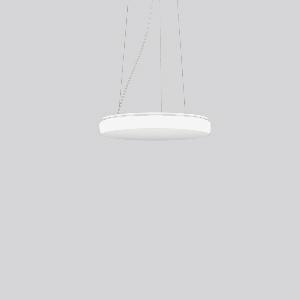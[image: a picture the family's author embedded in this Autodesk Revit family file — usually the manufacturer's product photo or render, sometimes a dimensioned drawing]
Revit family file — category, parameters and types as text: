
# Revit family: flat_polymero_kreis_slim_312090_002_2_f830
name_source: partatom
category: Lighting Fixtures
units: mm (PartAtom-declared; Revit-internal decimal feet)

## family parameters
Cut with Voids When Loaded = No
Host = Face
Light Source = No
Part Type = Normal
Room Calculation Point = No
Round Connector Dimension = Use Diameter
Shared = No

## types (1)
- FLAT POLYMERO KREIS SLIM (1 x LED Modul 830, 2000 lm, 3000)
    Apparent Load = 19 VA
    CIE Flux Codes = 44 76 94 92 100
    Color Rendering = 80
    Color Temperature = 3000
    Default Elevation = 1800 mm
    Description = Series: FLAT POLYMERO KREIS SLIM
Decorative round LED pendant luminaire. Base and canopy: metal, powder-coated, white. Canopy Ø 205 mm, h 35 mm. Diffuser made of plastic (polycarbonate), opal, shockproof. Diffuser fastening: patented push system. Homogeneous and smooth light distribution. Suitable for pendant. 3-point steel cable suspension, steplessly adjustable. Special lengths available on request. 
Colour: white
Diameter: 460 mm
Height: 68 mm
Suspension length: 200-1300 mm
Lamp: LED
Socket: without socket
Colour temperature: 3000K
Colour rendering index (CRI): 80
System power: 19 W
Rated luminous flux: 2000 lm
Luminous efficiency: 105 lm/W
Control gear: AC Strom, dim.Ph.an-/abschnitt
Protection class: I
Type of protection: IP 40
    Height = 68 mm
    Lamp = 1 x LED Modul 830
    Lamp Light Flux = 2000 lm
    Lamp count = 1
    Length = 460 mm
    Lifetime = 50000 h
    Luminous efficacy = 105 lm/W
    Manufacturer = RZB
    ModVariant = No
    Model = 312090.002.2
    Mounting Place = Ceiling
    Mounting Type = Pendant
    Number of Poles = 1
    OnlyDefault = Yes
    Power Factor = 1
    Product Name = FLAT POLYMERO KREIS SLIM
    Product group = Pendant luminaires
    ProductGroupID = 902
    Protection Class = Protection class I
    Protection Degree = IP 40
    RLX_Detail_Level = 1
    RLX_Emergency_Light_Flux = 0 lm
    RLX_Emergency_Type = 0
    RLX_Emergency_Type_DB = No
    RlxData = <blob elided: 58197 chars, md5=236e9bc3>
    Socket = socket
    Standby Power = 0 W
    System Light Flux = 2000 lm
    System Power = 19 W
    Type Comments = Product without accessories
    Type Image = 312090.002.jpg
    URL = http://relux.com
    VarID = ---
    Voltage = 230 V
    Voltage Range = 220-240 V
    Weight = 0.00 kg
    Width = 0 mm  [stored 0 ft]

note: [stored X ft] marks values corroborated as IEEE doubles in the binary element streams (Revit-internal decimal feet)

## geometry (parser evidence)
native form markers: Blend x4, Sweep x13
no freeform markers — native parametric forms only
